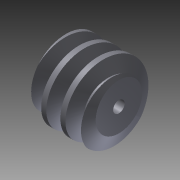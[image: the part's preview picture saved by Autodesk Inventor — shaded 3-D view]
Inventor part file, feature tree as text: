
AUTODESK INVENTOR PART (.ipt)
format: ipt  version: 2011 (Build 150239000, 239)  size: 249,856 bytes
history: native  units: mm (DEFAULTED — no unit token found)
features: other x6, chamfer x2, pattern_circular x2, extrude x1, hole x1, sketch x1
ambient origin geometry x6: Origin, XZ Plane, X Axis, Y Axis, Z Axis, Center Point
bodies: Solid1 (feature_tree)
feature tree (13):
  extrude  "Base Body"  Depth=4.026691mm
  chamfer  "Chamfer1"  Distance=5.0mm
  chamfer  "Chamfer2"  [1 undecoded]
  other  "Tooth Sketch"
  other  "Tooth"
  pattern_circular  "Tooth Pattern"  [2 undecoded]
  other  "Left Tooth"
  pattern_circular  "Left Tooth Pattern"  [2 undecoded]
  hole  "Hole1"  [1 undecoded]
  other  "Base Body Sketch"
  sketch  "Sketch5"  dims[d4=40.0mm d5=4.026691mm d6=5.0mm d7=0.0mm d8=0.268693mm d9=0.738227mm d10=0.268693mm d11=0.738227mm d12=19.198622mm d14=3.1425mm d24=19.198622mm d25=3.689648mm d26=0.263546mm d27=1.275119mm d28=1.677788mm d29=2.033479mm d30=1.054185mm d31=10.0mm d32=70.0mm d33=0.0mm d34=90.0deg d35=90.0deg d36=0.0mm d37=0.0mm d44=10.0mm d46=360.0deg d47=45.0deg d48=45.0deg d49=3.355575mm d50=0.0mm d54=0.0mm d56=0.0mm d59=3.355575mm d60=10.0mm d61=0.0mm d62=1.054185mm d63=10.0mm d64=70.0mm d65=0.0mm d66=90.0deg d67=90.0deg d68=0.0mm d69=0.0mm d70=10.0mm d71=10.0mm d72=10.0mm d73=360.0deg d75=10.0mm d76=10.0mm d77=0.0mm d79=3.355575mm d80=0.0mm d81=10.0mm d82=10.0mm d83=2.0mm d84=6.0mm d85=4.0mm d86=2.0mm d87=90.0deg d88=8.0mm d89=20.594885mm]
  other  "Srf1"
  other  "Pitch Diameter"
note: 6 required parameter values undecoded (feature->parameter linkage not recoverable at this tier; creation-order binding heuristic only, values carry confidence <= 0.55)
